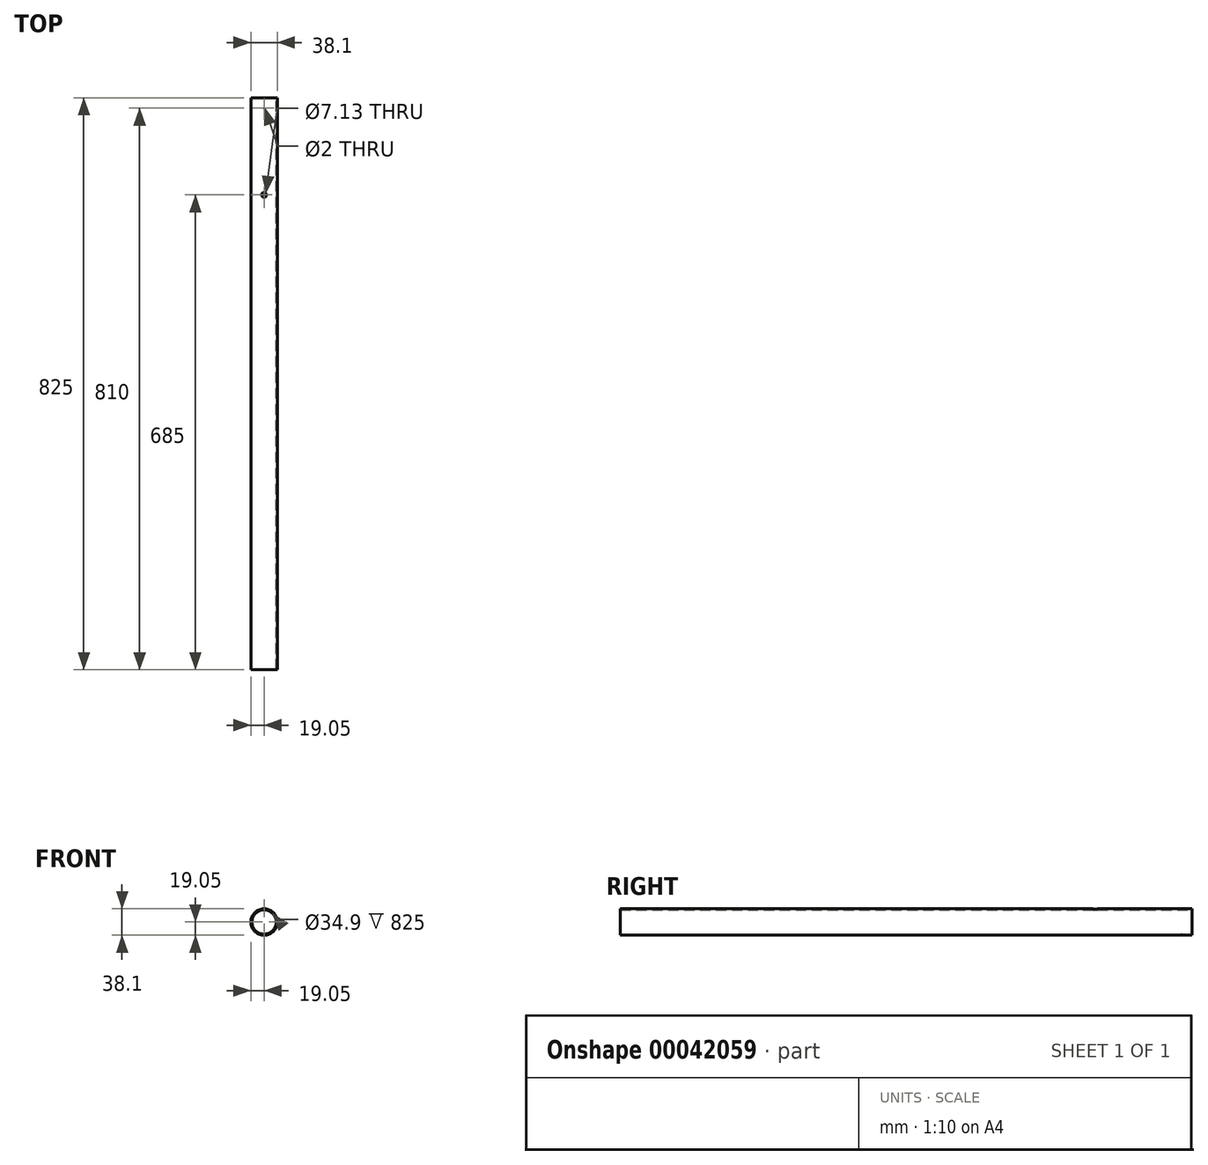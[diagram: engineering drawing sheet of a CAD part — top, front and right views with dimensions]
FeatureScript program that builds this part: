
annotation { "Feature Type Name" : "Feature", "Feature Type Description" : "" }
export const myFeature = defineFeature(function(context is Context, id is Id, definition is map)
    precondition{}
    {
        {
            var Q0;
            Q0=qCreatedBy(makeId("Front.planeOp"),FACE);
            var sketch = newSketch(context, id + "F0", { "sketchPlane" : qUnion([Q0])});
            skCircle(sketch, "E0", {"center": v(0, 0) * mm, "radius": 19.05 * mm});
            skCircle(sketch, "E1.0", {"center": v(0, 0) * mm, "radius": 17.45 * mm});
            skSolve(sketch);
        }
        {
            var Q0;
            Q0=makeQuery(id+"F0.imprint","IMPRINT",FACE,{"disambiguationData":[TD([[makeQuery(id+"F0.imprint","IMPRINT",EDGE,{"derivedFrom":sQuery(id+"F0.wireOp",EDGE,"E0")}),1.0]])]});
            extrude(context, id + "F1", {"entities" : qUnion([Q0]), "depth" : 825 * mm});
        }
        {
            var Q0;
            Q0=qCreatedBy(makeId("Top.planeOp"),FACE);
            var sketch = newSketch(context, id + "F2", { "sketchPlane" : qUnion([Q0])});
            skCircle(sketch, "E2", {"center": v(0, -140) * mm, "radius": 3.56 * mm});
            skSolve(sketch);
        }
        {
            var Q0;
            Q0 = qSketchRegion(id + "F2", true);
            var Q1;
            Q1=makeQuery(id+"F1.opExtrude","SWEPT_FACE",FACE,{"disambiguationData":[OSD([sQuery(id+"F0.wireOp",EDGE,"E0")])]});
            extrude(context, id + "F3", {"entities" : qUnion([Q0]), "operationType" : NewBodyOperationType.REMOVE, "endBound" : BoundingType.UP_TO_SURFACE, "endBoundEntityFace" : qUnion([Q1]), "depth" : 25 * mm});
        }
        {
            var Q0;
            Q0=qCreatedBy(makeId("Top.planeOp"),FACE);
            var sketch = newSketch(context, id + "F4", { "sketchPlane" : qUnion([Q0])});
            skCircle(sketch, "E3", {"center": v(0, -15) * mm, "radius": 1 * mm});
            skSolve(sketch);
        }
        {
            var Q0;
            Q0 = qSketchRegion(id + "F4", true);
            var Q1;
            Q1=makeQuery(id+"F1.opExtrude","SWEPT_FACE",FACE,{"disambiguationData":[OSD([sQuery(id+"F0.wireOp",EDGE,"E0")])]});
            extrude(context, id + "F5", {"entities" : qUnion([Q0]), "operationType" : NewBodyOperationType.REMOVE, "endBound" : BoundingType.UP_TO_SURFACE, "oppositeDirection" : true, "endBoundEntityFace" : qUnion([Q1]), "depth" : 25 * mm});
        }
    });
